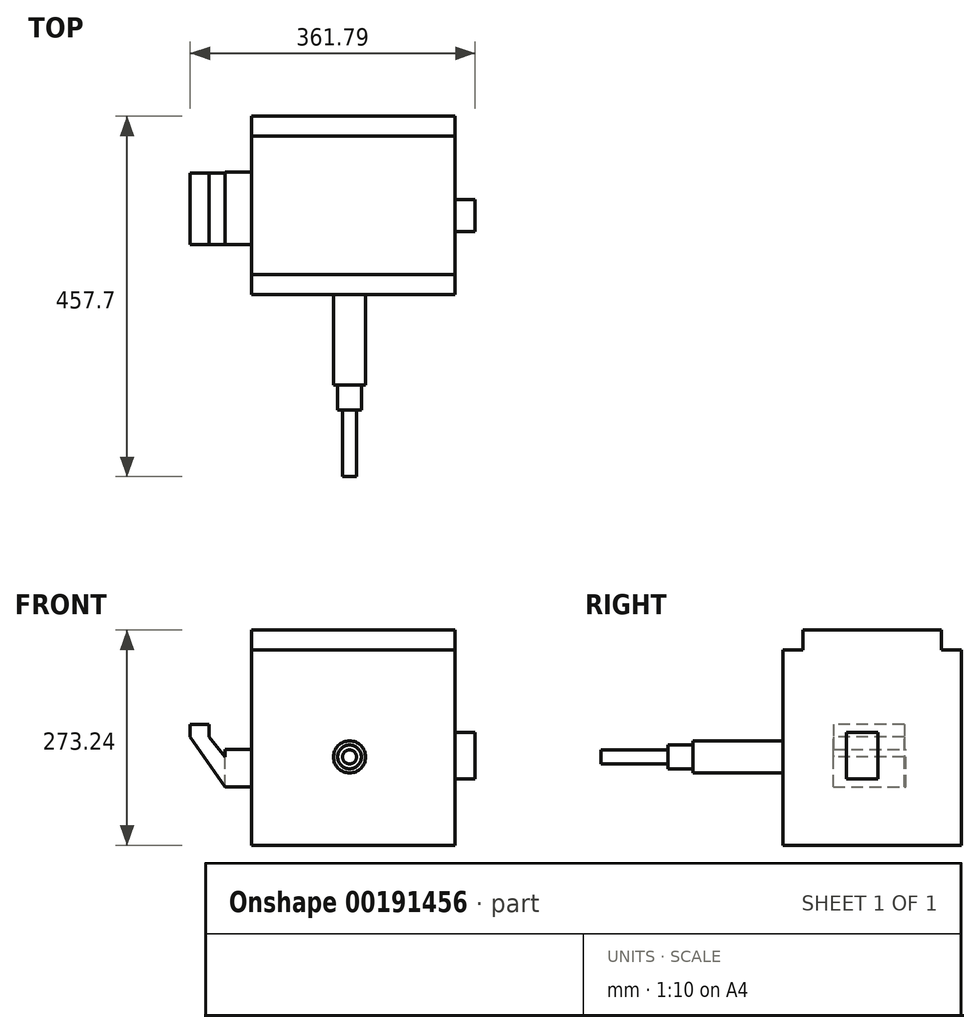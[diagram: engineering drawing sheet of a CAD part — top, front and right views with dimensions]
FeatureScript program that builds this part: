
annotation { "Feature Type Name" : "Feature", "Feature Type Description" : "" }
export const myFeature = defineFeature(function(context is Context, id is Id, definition is map)
    precondition{}
    {
        {
            var Q0;
            Q0=qCreatedBy(makeId("Front.planeOp"),FACE);
            var sketch = newSketch(context, id + "F0", { "sketchPlane" : qUnion([Q0])});
            skLineSegment(sketch, "E0.bottom", {"start": v(-72.7, 60.34) * mm, "end": v(72.7, 60.34) * mm});
            skLineSegment(sketch, "E0.top", {"start": v(-72.7, -60.34) * mm, "end": v(72.7, -60.34) * mm});
            skLineSegment(sketch, "E0.left", {"start": v(-72.7, 60.34) * mm, "end": v(-72.7, -60.34) * mm});
            skLineSegment(sketch, "E0.right", {"start": v(72.7, 60.34) * mm, "end": v(72.7, -60.34) * mm});
            skPoint(sketch, "E0.middle", {"position": v(0, 0) * mm});
            skLineSegment(sketch, "E1.bottom", {"start": v(-61.68, -60.34) * mm, "end": v(61.68, -60.34) * mm});
            skLineSegment(sketch, "E1.top", {"start": v(-61.68, -87.16) * mm, "end": v(61.68, -87.16) * mm});
            skLineSegment(sketch, "E1.left", {"start": v(-61.68, -60.34) * mm, "end": v(-61.68, -87.16) * mm});
            skLineSegment(sketch, "E1.right", {"start": v(61.68, -60.34) * mm, "end": v(61.68, -87.16) * mm});
            skPoint(sketch, "E1.middle", {"position": v(0, -73.75) * mm});
            skPoint(sketch, "E1.middle.positionSnap0", {"position": v(0, -60.34) * mm});
            skPoint(sketch, "E1.centerSnap0", {"position": v(0, -60.34) * mm});
            skCircle(sketch, "E2", {"center": v(0, 0) * mm, "radius": 20.38 * mm});
            skSolve(sketch);
        }
        {
            var Q0;
            Q0=makeQuery(id+"F0.imprint","IMPRINT",FACE,{"disambiguationData":[TD([[makeQuery(id+"F0.imprint","IMPRINT",EDGE,{"derivedFrom":sQuery(id+"F0.wireOp",EDGE,"E2")}),1.0]])]});
            extrude(context, id + "F1", {"entities" : qUnion([Q0]), "depth" : 114.8 * mm});
        }
        {
            var Q0;
            Q0=qCreatedBy(makeId("Front.planeOp"),FACE);
            var sketch = newSketch(context, id + "F2", { "sketchPlane" : qUnion([Q0])});
            skLineSegment(sketch, "E3.bottom", {"start": v(-64.07, 66.9) * mm, "end": v(64.07, 66.9) * mm});
            skLineSegment(sketch, "E3.top", {"start": v(-64.07, -66.9) * mm, "end": v(64.07, -66.9) * mm});
            skLineSegment(sketch, "E3.left", {"start": v(-64.07, 66.9) * mm, "end": v(-64.07, -66.9) * mm});
            skLineSegment(sketch, "E3.right", {"start": v(64.07, 66.9) * mm, "end": v(64.07, -66.9) * mm});
            skPoint(sketch, "E3.middle", {"position": v(0, 0) * mm});
            skSolve(sketch);
        }
        {
            var Q0;
            Q0 = qSketchRegion(id + "F2", true);
            extrude(context, id + "F3", {"entities" : qUnion([Q0]), "operationType" : NewBodyOperationType.ADD, "oppositeDirection" : true, "depth" : 158.24 * mm});
        }
        {
            var Q0;
            Q0=makeQuery(id+"F1.opExtrude","CAP_FACE",FACE,{"disambiguationData":[OSD([sQuery(id+"F0.wireOp",EDGE,"E2")])],"isStart":false});
            var sketch = newSketch(context, id + "F4", { "sketchPlane" : qUnion([Q0])});
            skCircle(sketch, "E4", {"center": v(0, 0) * mm, "radius": 15.17 * mm});
            skSolve(sketch);
        }
        {
            var Q0;
            Q0=makeQuery(id+"F4.imprint","IMPRINT",FACE,{"disambiguationData":[TD([[makeQuery(id+"F4.imprint","IMPRINT",EDGE,{"derivedFrom":sQuery(id+"F4.wireOp",EDGE,"E4")}),1.0]])]});
            extrude(context, id + "F5", {"entities" : qUnion([Q0]), "operationType" : NewBodyOperationType.ADD, "depth" : 31.75 * mm});
        }
        {
            var Q0;
            Q0=makeQuery(id+"F5.opExtrude","CAP_FACE",FACE,{"disambiguationData":[OSD([sQuery(id+"F4.wireOp",EDGE,"E4")])],"isStart":false});
            var sketch = newSketch(context, id + "F6", { "sketchPlane" : qUnion([Q0])});
            skCircle(sketch, "E5", {"center": v(0, 0) * mm, "radius": 8.92 * mm});
            skSolve(sketch);
        }
        {
            var Q0;
            Q0 = qSketchRegion(id + "F6", true);
            var Q1;
            Q1=makeQuery(id+"F6.imprint","IMPRINT",FACE,{"disambiguationData":[TD([[makeQuery(id+"F6.imprint","IMPRINT",EDGE,{"derivedFrom":sQuery(id+"F6.wireOp",EDGE,"E5")}),1.0]])]});
            extrude(context, id + "F7", {"entities" : qUnion([Q0, Q1]), "operationType" : NewBodyOperationType.ADD, "depth" : 84.84 * mm});
        }
        {
            var Q0;
            Q0=makeQuery(id+"F3.opExtrude","CAP_FACE",FACE,{"disambiguationData":[OSD([sQuery(id+"F2.wireOp",EDGE,"E3.bottom"),sQuery(id+"F2.wireOp",EDGE,"E3.top"),sQuery(id+"F2.wireOp",EDGE,"E3.left"),sQuery(id+"F2.wireOp",EDGE,"E3.right")])],"isStart":false});
            extrude(context, id + "F8", {"entities" : qUnion([Q0]), "operationType" : NewBodyOperationType.ADD, "depth" : 68.07 * mm});
        }
        {
            var Q0;
            {var subQ0=sQuery(id+"F2.wireOp",EDGE,"E3.bottom");Q0=makeQuery(id+"F8.boolean.opBoolean","MERGE",FACE,{"derivedFrom":[makeQuery(id+"F3.opExtrude","SWEPT_FACE",FACE,{"disambiguationData":[OSD([subQ0])]}),makeQuery(id+"F8.opExtrude","SWEPT_FACE",FACE,{"disambiguationData":[OSD([subQ0])]})]});}
            extrude(context, id + "F9", {"entities" : qUnion([Q0]), "operationType" : NewBodyOperationType.ADD, "depth" : 68.83 * mm});
        }
        {
            var Q0;
            {var subQ0=sQuery(id+"F2.wireOp",EDGE,"E3.top");Q0=makeQuery(id+"F8.boolean.opBoolean","MERGE",FACE,{"derivedFrom":[makeQuery(id+"F3.opExtrude","SWEPT_FACE",FACE,{"disambiguationData":[OSD([subQ0])]}),makeQuery(id+"F8.opExtrude","SWEPT_FACE",FACE,{"disambiguationData":[OSD([subQ0])]})]});}
            extrude(context, id + "F10", {"entities" : qUnion([Q0]), "operationType" : NewBodyOperationType.ADD, "depth" : 45.2 * mm});
        }
        {
            var Q0;
            {var subQ0=sQuery(id+"F2.wireOp",EDGE,"E3.right");Q0=makeQuery(id+"F10.boolean.opBoolean","MERGE",FACE,{"derivedFrom":[makeQuery(id+"F9.boolean.opBoolean","MERGE",FACE,{"derivedFrom":[makeQuery(id+"F8.boolean.opBoolean","MERGE",FACE,{"derivedFrom":[makeQuery(id+"F3.opExtrude","SWEPT_FACE",FACE,{"disambiguationData":[OSD([subQ0])]}),makeQuery(id+"F8.opExtrude","SWEPT_FACE",FACE,{"disambiguationData":[OSD([subQ0])]})]}),makeQuery(id+"F9.opExtrude","SWEPT_FACE",FACE,{"disambiguationData":[OSD([sQuery(id+"F2.wireOp",EDGE,"E3.bottom"),subQ0])]})]}),makeQuery(id+"F10.opExtrude","SWEPT_FACE",FACE,{"disambiguationData":[OSD([sQuery(id+"F2.wireOp",EDGE,"E3.top"),subQ0])]})]});}
            extrude(context, id + "F11", {"entities" : qUnion([Q0]), "operationType" : NewBodyOperationType.ADD, "depth" : 69.85 * mm});
        }
        {
            var Q0;
            {var subQ0=sQuery(id+"F2.wireOp",EDGE,"E3.left");Q0=makeQuery(id+"F10.boolean.opBoolean","MERGE",FACE,{"derivedFrom":[makeQuery(id+"F9.boolean.opBoolean","MERGE",FACE,{"derivedFrom":[makeQuery(id+"F8.boolean.opBoolean","MERGE",FACE,{"derivedFrom":[makeQuery(id+"F3.opExtrude","SWEPT_FACE",FACE,{"disambiguationData":[OSD([subQ0])]}),makeQuery(id+"F8.opExtrude","SWEPT_FACE",FACE,{"disambiguationData":[OSD([subQ0])]})]}),makeQuery(id+"F9.opExtrude","SWEPT_FACE",FACE,{"disambiguationData":[OSD([sQuery(id+"F2.wireOp",EDGE,"E3.bottom"),subQ0])]})]}),makeQuery(id+"F10.opExtrude","SWEPT_FACE",FACE,{"disambiguationData":[OSD([sQuery(id+"F2.wireOp",EDGE,"E3.top"),subQ0])]})]});}
            extrude(context, id + "F12", {"entities" : qUnion([Q0]), "operationType" : NewBodyOperationType.ADD, "depth" : 60.7 * mm});
        }
        {
            var Q0;
            Q0=makeQuery(id+"F12.opExtrude","CAP_FACE",FACE,{"disambiguationData":[OSD([sQuery(id+"F2.wireOp",EDGE,"E3.bottom"),sQuery(id+"F2.wireOp",EDGE,"E3.top"),sQuery(id+"F2.wireOp",EDGE,"E3.left")])],"isStart":false});
            var sketch = newSketch(context, id + "F13", { "sketchPlane" : qUnion([Q0])});
            skLineSegment(sketch, "E6.bottom", {"start": v(-63.62, -37.97) * mm, "end": v(-155.76, -37.97) * mm});
            skLineSegment(sketch, "E6.top", {"start": v(-63.62, 9.58) * mm, "end": v(-155.76, 9.58) * mm});
            skLineSegment(sketch, "E6.left", {"start": v(-63.62, -37.97) * mm, "end": v(-63.62, 9.58) * mm});
            skLineSegment(sketch, "E6.right", {"start": v(-155.76, -37.97) * mm, "end": v(-155.76, 9.58) * mm});
            skSolve(sketch);
        }
        {
            var Q0;
            Q0=makeQuery(id+"F13.imprint","IMPRINT",FACE,{"disambiguationData":[TD([[makeQuery(id+"F13.imprint","IMPRINT",EDGE,{"derivedFrom":sQuery(id+"F13.wireOp",EDGE,"E6.bottom")}),-1.0]])]});
            extrude(context, id + "F14", {"entities" : qUnion([Q0]), "operationType" : NewBodyOperationType.ADD, "depth" : 33.53 * mm});
        }
        {
            var Q0;
            Q0=makeQuery(id+"F14.opExtrude","SWEPT_FACE",FACE,{"disambiguationData":[OSD([sQuery(id+"F13.wireOp",EDGE,"E6.left")])]});
            var sketch = newSketch(context, id + "F15", { "sketchPlane" : qUnion([Q0])});
            skLineSegment(sketch, "E7", {"start": v(-158.3, -37.97) * mm, "end": v(-202.47, 25.19) * mm});
            skLineSegment(sketch, "E8", {"start": v(-202.47, 25.19) * mm, "end": v(-202.47, 41.53) * mm});
            skLineSegment(sketch, "E9", {"start": v(-202.47, 41.53) * mm, "end": v(-178.2, 41.53) * mm});
            skLineSegment(sketch, "E10", {"start": v(-178.2, 41.53) * mm, "end": v(-178.2, 25.19) * mm});
            skLineSegment(sketch, "E11", {"start": v(-178.2, 25.19) * mm, "end": v(-158.3, 0) * mm});
            skSolve(sketch);
        }
        {
            var Q0;
            {var subQ0=sQuery(id+"F15.wireOp",EDGE,"E7");Q0=makeQuery(id+"F15.imprint","IMPRINT",FACE,{"disambiguationData":[TD([[makeQuery(id+"F15.imprint","IMPRINT",EDGE,{"derivedFrom":subQ0}),-1.0]])]});}
            extrude(context, id + "F16", {"entities" : qUnion([Q0]), "operationType" : NewBodyOperationType.ADD, "oppositeDirection" : true, "depth" : 90.42 * mm});
        }
        {
            var Q0;
            Q0=makeQuery(id+"F11.opExtrude","CAP_FACE",FACE,{"disambiguationData":[OSD([sQuery(id+"F2.wireOp",EDGE,"E3.bottom"),sQuery(id+"F2.wireOp",EDGE,"E3.top"),sQuery(id+"F2.wireOp",EDGE,"E3.right")])],"isStart":false});
            var sketch = newSketch(context, id + "F17", { "sketchPlane" : qUnion([Q0])});
            skLineSegment(sketch, "E12.bottom", {"start": v(80.13, -28.2) * mm, "end": v(120.75, -28.2) * mm});
            skLineSegment(sketch, "E12.top", {"start": v(80.13, 31.24) * mm, "end": v(120.75, 31.24) * mm});
            skLineSegment(sketch, "E12.left", {"start": v(80.13, -28.2) * mm, "end": v(80.13, 31.24) * mm});
            skLineSegment(sketch, "E12.right", {"start": v(120.75, -28.2) * mm, "end": v(120.75, 31.24) * mm});
            skSolve(sketch);
        }
        {
            var Q0;
            Q0 = qSketchRegion(id + "F17", true);
            extrude(context, id + "F18", {"entities" : qUnion([Q0]), "operationType" : NewBodyOperationType.ADD, "depth" : 25.4 * mm});
        }
        {
            var Q0;
            {var subQ0=sQuery(id+"F2.wireOp",EDGE,"E3.bottom");Q0=makeQuery(id+"F12.boolean.opBoolean","MERGE",FACE,{"derivedFrom":[makeQuery(id+"F11.boolean.opBoolean","MERGE",FACE,{"derivedFrom":[makeQuery(id+"F9.opExtrude","CAP_FACE",FACE,{"disambiguationData":[OSD([subQ0])],"isStart":false}),makeQuery(id+"F11.opExtrude","SWEPT_FACE",FACE,{"disambiguationData":[OSD([subQ0,sQuery(id+"F2.wireOp",EDGE,"E3.right")])]})]}),makeQuery(id+"F12.opExtrude","SWEPT_FACE",FACE,{"disambiguationData":[OSD([subQ0,sQuery(id+"F2.wireOp",EDGE,"E3.left")])]})]});}
            var sketch = newSketch(context, id + "F19", { "sketchPlane" : qUnion([Q0])});
            skLineSegment(sketch, "E13.bottom", {"start": v(-124.77, 25.04) * mm, "end": v(133.92, 25.04) * mm});
            skLineSegment(sketch, "E13.top", {"start": v(-124.77, 201.39) * mm, "end": v(133.92, 201.39) * mm});
            skLineSegment(sketch, "E13.left", {"start": v(-124.77, 25.04) * mm, "end": v(-124.77, 201.39) * mm});
            skLineSegment(sketch, "E13.right", {"start": v(133.92, 25.04) * mm, "end": v(133.92, 201.39) * mm});
            skSolve(sketch);
        }
        {
            var Q0;
            Q0=makeQuery(id+"F19.imprint","IMPRINT",FACE,{"disambiguationData":[TD([[makeQuery(id+"F19.imprint","IMPRINT",EDGE,{"derivedFrom":sQuery(id+"F19.wireOp",EDGE,"E13.bottom")}),1.0]])]});
            extrude(context, id + "F20", {"entities" : qUnion([Q0]), "operationType" : NewBodyOperationType.ADD, "depth" : 25.4 * mm});
        }
    });
